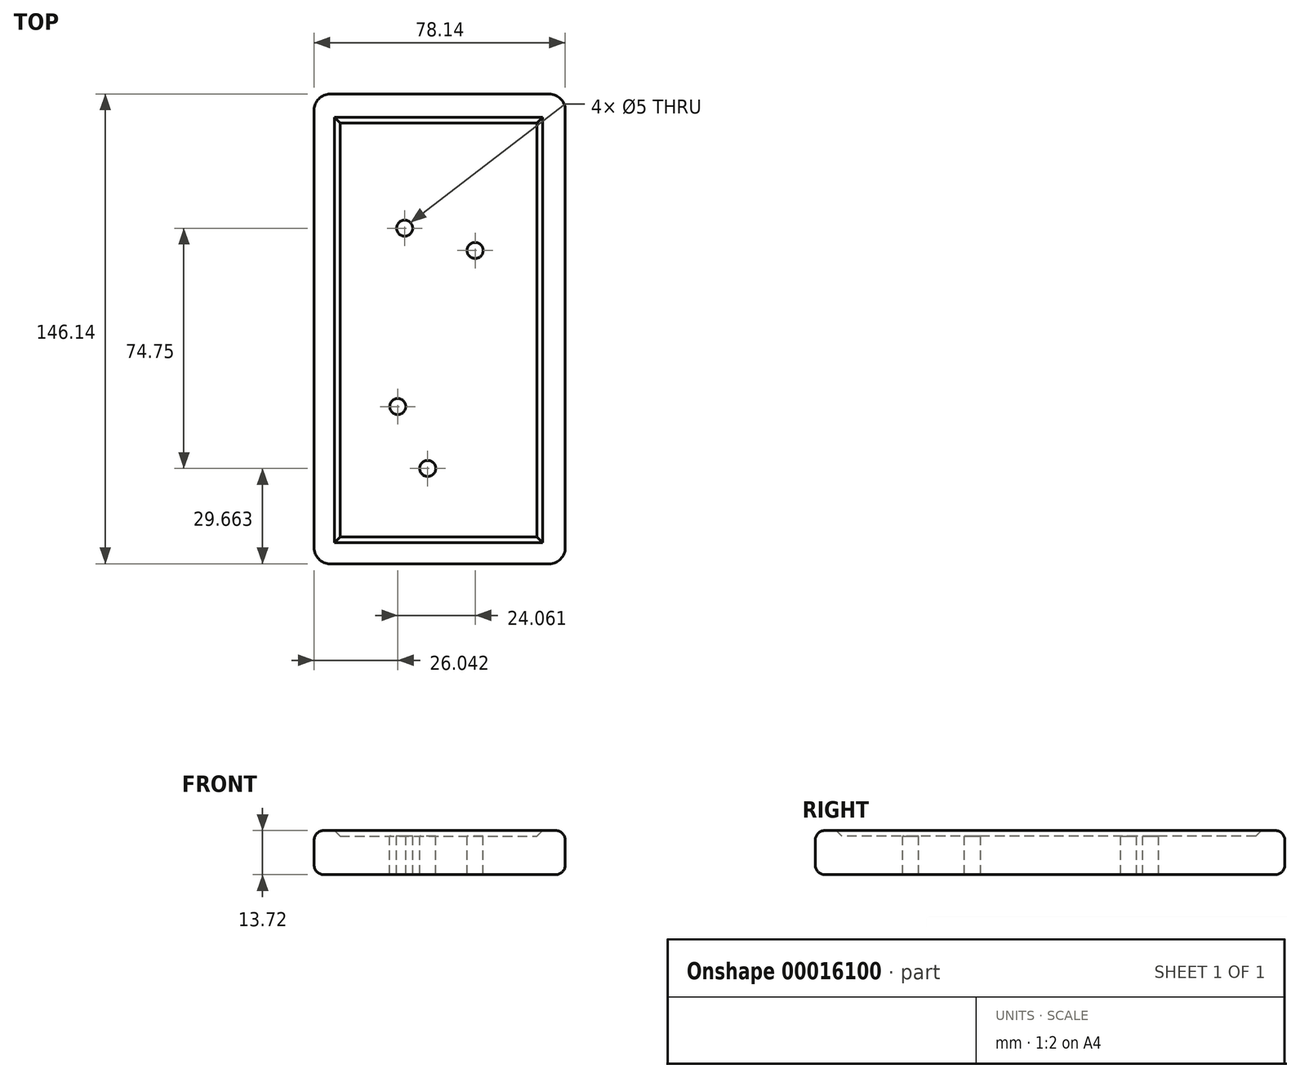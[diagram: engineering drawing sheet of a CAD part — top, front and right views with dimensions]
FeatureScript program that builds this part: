
annotation { "Feature Type Name" : "Feature", "Feature Type Description" : "" }
export const myFeature = defineFeature(function(context is Context, id is Id, definition is map)
    precondition{}
    {
        {
            var Q0;
            Q0=qCreatedBy(makeId("Top.planeOp"),FACE);
            var sketch = newSketch(context, id + "F0", { "sketchPlane" : qUnion([Q0])});
            skLineSegment(sketch, "E0.rect.bottom", {"start": v(40.65, -73.07) * mm, "end": v(-37.49, -73.07) * mm});
            skLineSegment(sketch, "E0.rect.top", {"start": v(40.65, 73.07) * mm, "end": v(-37.49, 73.07) * mm});
            skLineSegment(sketch, "E0.rect.left", {"start": v(40.65, -73.07) * mm, "end": v(40.65, 73.07) * mm});
            skLineSegment(sketch, "E0.rect.right", {"start": v(-37.49, -73.07) * mm, "end": v(-37.49, 73.07) * mm});
            skPoint(sketch, "E0.rect.middle", {"position": v(1.58, 0) * mm});
            skSolve(sketch);
        }
        {
            var Q0;
            Q0=makeQuery(id+"F0.imprint","IMPRINT",FACE,{"disambiguationData":[TD([[makeQuery(id+"F0.imprint","IMPRINT",EDGE,{"derivedFrom":sQuery(id+"F0.wireOp",EDGE,"E0.rect.bottom")}),-1.0]])]});
            extrude(context, id + "F1", {"entities" : qUnion([Q0]), "depth" : 13.72 * mm});
        }
        {
            var Q0;
            Q0=makeQuery(id+"F1.opExtrude","CAP_FACE",FACE,{"disambiguationData":[OSD([sQuery(id+"F0.wireOp",EDGE,"E0.rect.bottom"),sQuery(id+"F0.wireOp",EDGE,"E0.rect.top"),sQuery(id+"F0.wireOp",EDGE,"E0.rect.left"),sQuery(id+"F0.wireOp",EDGE,"E0.rect.right")])],"isStart":false});
            var sketch = newSketch(context, id + "F2", { "sketchPlane" : qUnion([Q0])});
            skLineSegment(sketch, "E1.bottom", {"start": v(-34.38, 69.04) * mm, "end": v(36.86, 69.04) * mm});
            skLineSegment(sketch, "E1.top", {"start": v(-34.38, -69.77) * mm, "end": v(36.86, -69.77) * mm});
            skLineSegment(sketch, "E1.left", {"start": v(-34.38, 69.04) * mm, "end": v(-34.38, -69.77) * mm});
            skLineSegment(sketch, "E1.right", {"start": v(36.86, 69.04) * mm, "end": v(36.86, -69.77) * mm});
            skSolve(sketch);
        }
        {
            var Q0;
            Q0=makeQuery(id+"F2.imprint","IMPRINT",FACE,{"disambiguationData":[TD([[makeQuery(id+"F2.imprint","IMPRINT",EDGE,{"derivedFrom":sQuery(id+"F2.wireOp",EDGE,"E1.bottom")}),-1.0]])]});
            extrude(context, id + "F3", {"entities" : qUnion([Q0]), "operationType" : NewBodyOperationType.REMOVE, "oppositeDirection" : true, "depth" : 1.77 * mm});
        }
        {
            var Q0;
            Q0=makeQuery(id+"F3.boolean.opBoolean","COPY",EDGE,{"derivedFrom":makeQuery(id+"F3.opExtrude","CAP_EDGE",EDGE,{"disambiguationData":[OSD([sQuery(id+"F2.wireOp",EDGE,"E1.bottom")])],"isStart":false})});
            var Q1;
            Q1=makeQuery(id+"F3.boolean.opBoolean","COPY",EDGE,{"derivedFrom":makeQuery(id+"F3.opExtrude","CAP_EDGE",EDGE,{"disambiguationData":[OSD([sQuery(id+"F2.wireOp",EDGE,"E1.right")])],"isStart":false})});
            var Q2;
            Q2=makeQuery(id+"F3.boolean.opBoolean","COPY",EDGE,{"derivedFrom":makeQuery(id+"F3.opExtrude","CAP_EDGE",EDGE,{"disambiguationData":[OSD([sQuery(id+"F2.wireOp",EDGE,"E1.left")])],"isStart":false})});
            var Q3;
            Q3=makeQuery(id+"F3.boolean.opBoolean","COPY",EDGE,{"derivedFrom":makeQuery(id+"F3.opExtrude","CAP_EDGE",EDGE,{"disambiguationData":[OSD([sQuery(id+"F2.wireOp",EDGE,"E1.top")])],"isStart":false})});
            chamfer(context, id + "F4", {"entities" : qUnion([Q0, Q1, Q2, Q3]), "width" : 5 * mm, "tangentPropagation" : true});
        }
        {
            var Q0;
            Q0=makeQuery(id+"F1.opExtrude","CAP_EDGE",EDGE,{"disambiguationData":[OSD([sQuery(id+"F0.wireOp",EDGE,"E0.rect.right")])],"isStart":false});
            var Q1;
            Q1=makeQuery(id+"F1.opExtrude","CAP_EDGE",EDGE,{"disambiguationData":[OSD([sQuery(id+"F0.wireOp",EDGE,"E0.rect.top")])],"isStart":false});
            var Q2;
            Q2=makeQuery(id+"F1.opExtrude","CAP_EDGE",EDGE,{"disambiguationData":[OSD([sQuery(id+"F0.wireOp",EDGE,"E0.rect.left")])],"isStart":false});
            var Q3;
            Q3=makeQuery(id+"F1.opExtrude","CAP_EDGE",EDGE,{"disambiguationData":[OSD([sQuery(id+"F0.wireOp",EDGE,"E0.rect.bottom")])],"isStart":false});
            var Q4;
            Q4=makeQuery(id+"F1.opExtrude","CAP_FACE",FACE,{"disambiguationData":[OSD([sQuery(id+"F0.wireOp",EDGE,"E0.rect.bottom"),sQuery(id+"F0.wireOp",EDGE,"E0.rect.top"),sQuery(id+"F0.wireOp",EDGE,"E0.rect.left"),sQuery(id+"F0.wireOp",EDGE,"E0.rect.right")])],"isStart":true});
            fillet(context, id + "F5", {"entities" : qUnion([Q0, Q1, Q2, Q3, Q4]), "radius" : 3 * mm, "tangentPropagation" : true, "allowEdgeOverflow" : false});
        }
        {
            var Q0;
            Q0=makeQuery(id+"F1.opExtrude","SWEPT_EDGE",EDGE,{"disambiguationData":[OSD([sQuery(id+"F0.wireOp",EDGE,"E0.rect.bottom"),sQuery(id+"F0.wireOp",EDGE,"E0.rect.right")])]});
            var Q1;
            Q1=makeQuery(id+"F1.opExtrude","SWEPT_EDGE",EDGE,{"disambiguationData":[OSD([sQuery(id+"F0.wireOp",EDGE,"E0.rect.bottom"),sQuery(id+"F0.wireOp",EDGE,"E0.rect.left")])]});
            var Q2;
            Q2=makeQuery(id+"F1.opExtrude","SWEPT_EDGE",EDGE,{"disambiguationData":[OSD([sQuery(id+"F0.wireOp",EDGE,"E0.rect.top"),sQuery(id+"F0.wireOp",EDGE,"E0.rect.right")])]});
            var Q3;
            Q3=makeQuery(id+"F1.opExtrude","SWEPT_EDGE",EDGE,{"disambiguationData":[OSD([sQuery(id+"F0.wireOp",EDGE,"E0.rect.top"),sQuery(id+"F0.wireOp",EDGE,"E0.rect.left")])]});
            fillet(context, id + "F6", {"entities" : qUnion([Q0, Q1, Q2, Q3]), "radius" : 5 * mm, "tangentPropagation" : true, "allowEdgeOverflow" : false});
        }
        {
            var Q0;
            Q0=makeQuery(id+"F3.boolean.opBoolean","COPY",FACE,{"derivedFrom":makeQuery(id+"F3.opExtrude","CAP_FACE",FACE,{"disambiguationData":[OSD([sQuery(id+"F2.wireOp",EDGE,"E1.bottom"),sQuery(id+"F2.wireOp",EDGE,"E1.top"),sQuery(id+"F2.wireOp",EDGE,"E1.left"),sQuery(id+"F2.wireOp",EDGE,"E1.right")])],"isStart":false})});
            var sketch = newSketch(context, id + "F7", { "sketchPlane" : qUnion([Q0])});
            skPoint(sketch, "E2", {"position": v(-9.3, 31.34) * mm});
            skPoint(sketch, "E3", {"position": v(12.61, 24.41) * mm});
            skPoint(sketch, "E4", {"position": v(-2.13, -43.4) * mm});
            skPoint(sketch, "E5", {"position": v(-11.45, -24.14) * mm});
            skSolve(sketch);
        }
        {
            var Q0;
            Q0=sQuery(id+"F7.wireOp",VERTEX,"E2");
            var Q1;
            Q1=sQuery(id+"F7.wireOp",VERTEX,"E3");
            var Q2;
            Q2=sQuery(id+"F7.wireOp",VERTEX,"E5");
            var Q3;
            Q3=sQuery(id+"F7.wireOp",VERTEX,"E4");
            var Q4;
            Q4=makeQuery(id+"F1.opExtrude","SWEPT_BODY",BODY,{"disambiguationData":[OSD([sQuery(id+"F0.wireOp",EDGE,"E0.rect.bottom"),sQuery(id+"F0.wireOp",EDGE,"E0.rect.top"),sQuery(id+"F0.wireOp",EDGE,"E0.rect.left"),sQuery(id+"F0.wireOp",EDGE,"E0.rect.right")])]});
            hole(context, id + "F8", {"style" : HoleStyle.SIMPLE, "holeDiameter" : 5 * mm, "endStyle" : HoleEndStyle.THROUGH, "locations" : qUnion([Q0, Q1, Q2, Q3]), "scope" : qUnion([Q4])});
        }
    });
